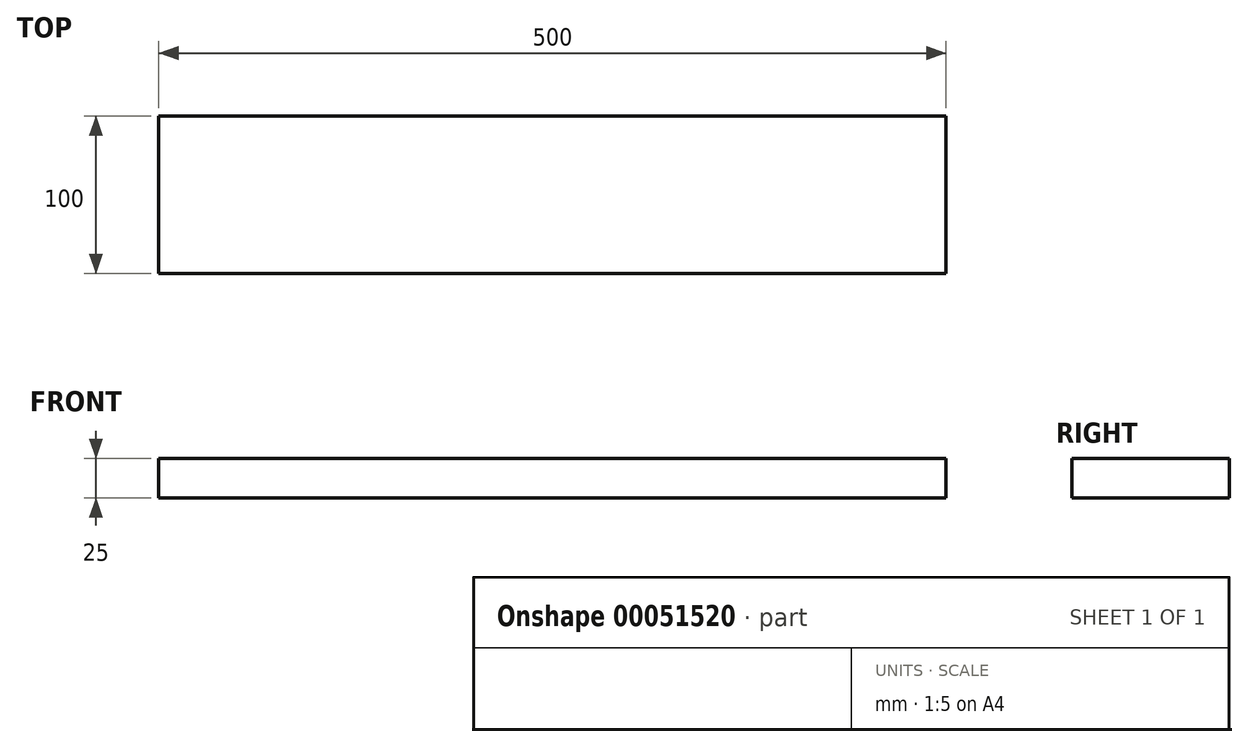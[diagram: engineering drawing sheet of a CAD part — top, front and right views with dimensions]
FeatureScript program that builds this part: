
annotation { "Feature Type Name" : "Feature", "Feature Type Description" : "" }
export const myFeature = defineFeature(function(context is Context, id is Id, definition is map)
    precondition{}
    {
        {
            var Q0;
            Q0=qCreatedBy(makeId("Top.planeOp"),FACE);
            var sketch = newSketch(context, id + "F0", { "sketchPlane" : qUnion([Q0])});
            skLineSegment(sketch, "E0.bottom", {"start": v(-51.38, 50) * mm, "end": v(448.62, 50) * mm});
            skLineSegment(sketch, "E0.top", {"start": v(-51.38, -50) * mm, "end": v(448.62, -50) * mm});
            skLineSegment(sketch, "E0.left", {"start": v(-51.38, 50) * mm, "end": v(-51.38, -50) * mm});
            skLineSegment(sketch, "E0.right", {"start": v(448.62, 50) * mm, "end": v(448.62, -50) * mm});
            skSolve(sketch);
        }
        {
            var Q0;
            Q0=qSketchRegion(id+"F0",true);
            extrude(context, id + "F1", {"entities" : qUnion([Q0]), "depth" : 25 * mm});
        }
    });
